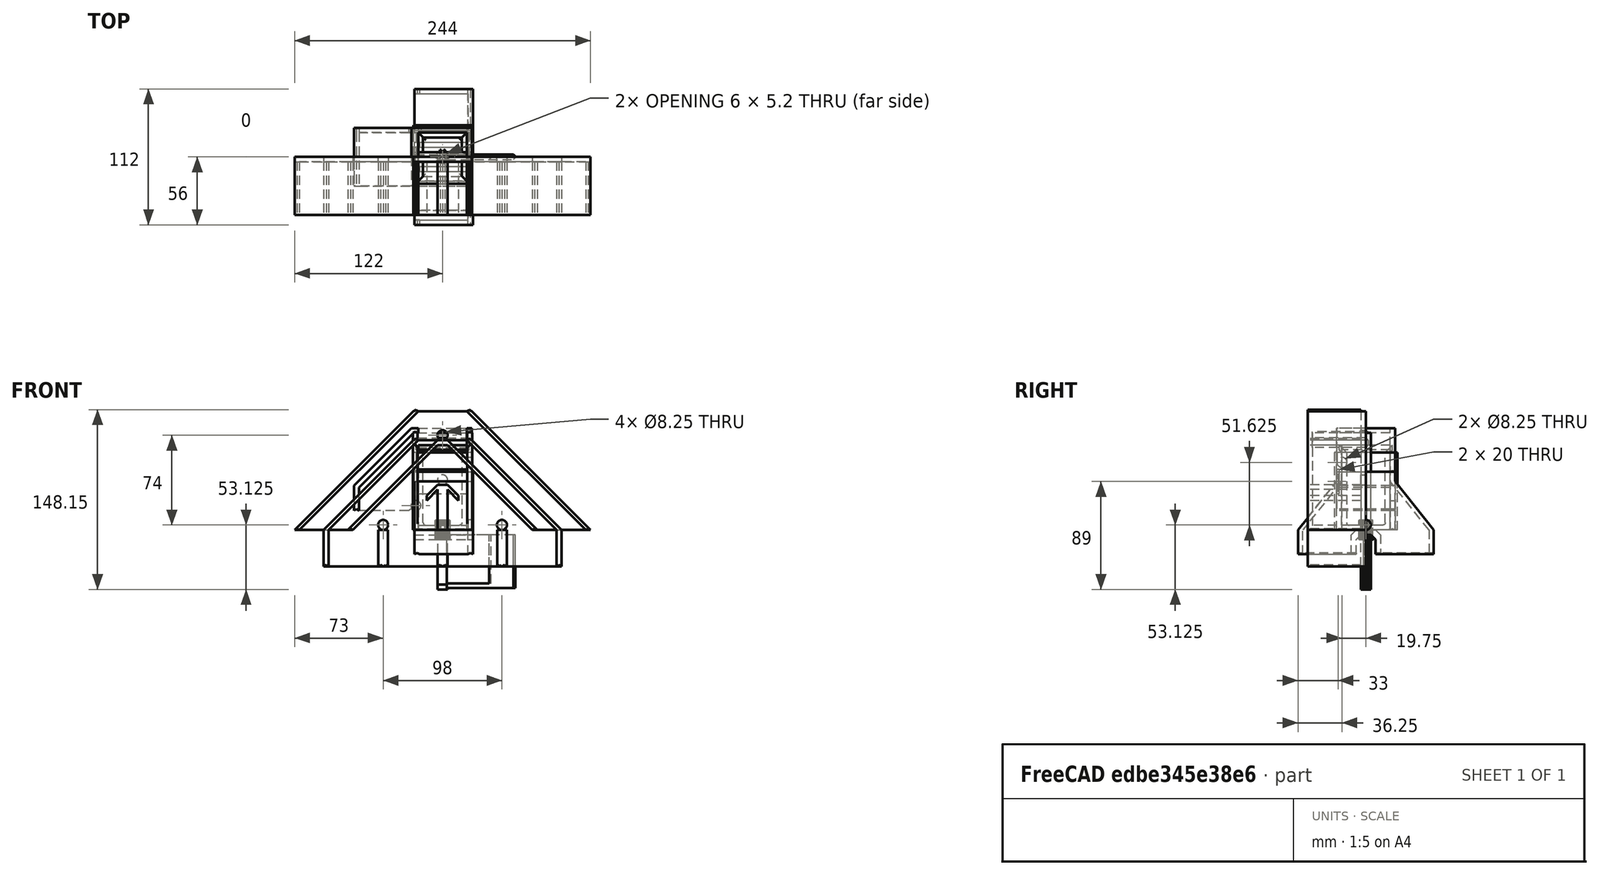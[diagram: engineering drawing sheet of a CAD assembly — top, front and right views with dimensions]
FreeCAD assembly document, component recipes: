
FREECAD ASSEMBLY — COMPONENT RECIPES ("Sorter")

This assembly document has 58 components, labeled P0..P57 below (a component is one placed body or linked part). 0 of them carry a construction recipe — the FreeCAD feature program that regenerates the part from scratch, quoted from this document or its linked companion documents; the rest are supplied as boundary geometry only. No exploded tour is included for this assembly.
COMPONENT P0 — geometry summary ("Bin001"; no construction recipe available for this part):
  bounding box: 70.0 x 44.0 x 44.0 mm
  tessellated surface: 356 triangles
  volume: 43396 mm^3 (32% of its bounding box)
  symmetry: 2-fold rotationally symmetric about the z axis; mirror-symmetric across its y mid-plane
COMPONENT P1 — geometry summary ("Bin002"; no construction recipe available for this part):
  bounding box: 70.0 x 44.0 x 44.0 mm
  tessellated surface: 356 triangles
  volume: 43396 mm^3 (32% of its bounding box)
  symmetry: 2-fold rotationally symmetric about the z axis; mirror-symmetric across its y mid-plane
COMPONENT P2 — geometry summary ("Bin003"; no construction recipe available for this part):
  bounding box: 70.0 x 44.0 x 44.0 mm
  tessellated surface: 356 triangles
  volume: 43396 mm^3 (32% of its bounding box)
  symmetry: 2-fold rotationally symmetric about the z axis; mirror-symmetric across its y mid-plane
COMPONENT P3 — geometry summary ("Bin004"; no construction recipe available for this part):
  bounding box: 70.0 x 44.0 x 44.0 mm
  tessellated surface: 356 triangles
  volume: 43396 mm^3 (32% of its bounding box)
  symmetry: 2-fold rotationally symmetric about the z axis; mirror-symmetric across its y mid-plane
COMPONENT P4 — geometry summary ("Bin005"; no construction recipe available for this part):
  bounding box: 70.0 x 44.0 x 44.0 mm
  tessellated surface: 356 triangles
  volume: 43396 mm^3 (32% of its bounding box)
  symmetry: 2-fold rotationally symmetric about the z axis; mirror-symmetric across its y mid-plane
COMPONENT P5 — geometry summary ("Bin006"; no construction recipe available for this part):
  bounding box: 70.0 x 44.0 x 44.0 mm
  tessellated surface: 356 triangles
  volume: 43396 mm^3 (32% of its bounding box)
  symmetry: 2-fold rotationally symmetric about the z axis; mirror-symmetric across its y mid-plane
COMPONENT P6 — geometry summary ("Bin007"; no construction recipe available for this part):
  bounding box: 70.0 x 44.0 x 44.0 mm
  tessellated surface: 356 triangles
  volume: 43396 mm^3 (32% of its bounding box)
  symmetry: 2-fold rotationally symmetric about the z axis; mirror-symmetric across its y mid-plane
COMPONENT P7 — geometry summary ("Bin008"; no construction recipe available for this part):
  bounding box: 70.0 x 44.0 x 44.0 mm
  tessellated surface: 356 triangles
  volume: 43396 mm^3 (32% of its bounding box)
  symmetry: 2-fold rotationally symmetric about the z axis; mirror-symmetric across its y mid-plane
COMPONENT P8 — geometry summary ("Bin009"; no construction recipe available for this part):
  bounding box: 70.0 x 44.0 x 44.0 mm
  tessellated surface: 356 triangles
  volume: 43396 mm^3 (32% of its bounding box)
  symmetry: 2-fold rotationally symmetric about the z axis; mirror-symmetric across its y mid-plane
COMPONENT P9 — geometry summary ("Bin010"; no construction recipe available for this part):
  bounding box: 70.0 x 44.0 x 44.0 mm
  tessellated surface: 356 triangles
  volume: 43396 mm^3 (32% of its bounding box)
  symmetry: 2-fold rotationally symmetric about the z axis; mirror-symmetric across its y mid-plane
COMPONENT P10 — geometry summary ("Bin011"; no construction recipe available for this part):
  bounding box: 70.0 x 44.0 x 44.0 mm
  tessellated surface: 356 triangles
  volume: 43396 mm^3 (32% of its bounding box)
  symmetry: 2-fold rotationally symmetric about the z axis; mirror-symmetric across its y mid-plane
COMPONENT P11 — geometry summary ("Bin012"; no construction recipe available for this part):
  bounding box: 70.0 x 44.0 x 44.0 mm
  tessellated surface: 356 triangles
  volume: 43396 mm^3 (32% of its bounding box)
  symmetry: 2-fold rotationally symmetric about the z axis; mirror-symmetric across its y mid-plane
COMPONENT P12 — geometry summary ("Bin013"; no construction recipe available for this part):
  bounding box: 70.0 x 44.0 x 44.0 mm
  tessellated surface: 356 triangles
  volume: 43396 mm^3 (32% of its bounding box)
  symmetry: 2-fold rotationally symmetric about the z axis; mirror-symmetric across its y mid-plane
COMPONENT P13 — geometry summary ("Bin014"; no construction recipe available for this part):
  bounding box: 70.0 x 44.0 x 44.0 mm
  tessellated surface: 356 triangles
  volume: 43396 mm^3 (32% of its bounding box)
  symmetry: 2-fold rotationally symmetric about the z axis; mirror-symmetric across its y mid-plane
COMPONENT P14 — geometry summary ("Bin015"; no construction recipe available for this part):
  bounding box: 70.0 x 44.0 x 44.0 mm
  tessellated surface: 356 triangles
  volume: 43396 mm^3 (32% of its bounding box)
  symmetry: 2-fold rotationally symmetric about the z axis; mirror-symmetric across its y mid-plane
COMPONENT P15 — geometry summary ("Bin016"; no construction recipe available for this part):
  bounding box: 70.0 x 44.0 x 44.0 mm
  tessellated surface: 356 triangles
  volume: 43396 mm^3 (32% of its bounding box)
  symmetry: 2-fold rotationally symmetric about the z axis; mirror-symmetric across its y mid-plane
COMPONENT P16 — geometry summary ("Bin017"; no construction recipe available for this part):
  bounding box: 70.0 x 44.0 x 44.0 mm
  tessellated surface: 356 triangles
  volume: 43396 mm^3 (32% of its bounding box)
  symmetry: 2-fold rotationally symmetric about the z axis; mirror-symmetric across its y mid-plane
COMPONENT P17 — geometry summary ("Bin Holder001"; no construction recipe available for this part):
  bounding box: 81.2 x 49.0 x 48.0 mm
  tessellated surface: 164 triangles
  volume: 49705 mm^3 (26% of its bounding box)
  symmetry: mirror-symmetric across its x mid-plane
COMPONENT P18 — geometry summary ("Bin Holder002"; no construction recipe available for this part):
  bounding box: 81.2 x 49.0 x 48.0 mm
  tessellated surface: 164 triangles
  volume: 49705 mm^3 (26% of its bounding box)
  symmetry: mirror-symmetric across its x mid-plane
COMPONENT P19 — geometry summary ("Bin Holder003"; no construction recipe available for this part):
  bounding box: 81.2 x 49.0 x 48.0 mm
  tessellated surface: 164 triangles
  volume: 49705 mm^3 (26% of its bounding box)
  symmetry: mirror-symmetric across its x mid-plane
COMPONENT P20 — geometry summary ("Bin Holder004"; no construction recipe available for this part):
  bounding box: 81.2 x 49.0 x 48.0 mm
  tessellated surface: 164 triangles
  volume: 49705 mm^3 (26% of its bounding box)
  symmetry: mirror-symmetric across its x mid-plane
COMPONENT P21 — geometry summary ("Bin Holder005"; no construction recipe available for this part):
  bounding box: 81.2 x 49.0 x 48.0 mm
  tessellated surface: 164 triangles
  volume: 49705 mm^3 (26% of its bounding box)
  symmetry: mirror-symmetric across its x mid-plane
COMPONENT P22 — geometry summary ("Bin Holder006"; no construction recipe available for this part):
  bounding box: 81.2 x 49.0 x 48.0 mm
  tessellated surface: 164 triangles
  volume: 49705 mm^3 (26% of its bounding box)
  symmetry: mirror-symmetric across its x mid-plane
COMPONENT P23 — geometry summary ("Bin Holder007"; no construction recipe available for this part):
  bounding box: 81.2 x 49.0 x 48.0 mm
  tessellated surface: 164 triangles
  volume: 49705 mm^3 (26% of its bounding box)
  symmetry: mirror-symmetric across its x mid-plane
COMPONENT P24 — geometry summary ("Bin Holder008"; no construction recipe available for this part):
  bounding box: 81.2 x 49.0 x 48.0 mm
  tessellated surface: 164 triangles
  volume: 49705 mm^3 (26% of its bounding box)
  symmetry: mirror-symmetric across its x mid-plane
COMPONENT P25 — geometry summary ("Bin Holder009"; no construction recipe available for this part):
  bounding box: 81.2 x 49.0 x 48.0 mm
  tessellated surface: 164 triangles
  volume: 49705 mm^3 (26% of its bounding box)
  symmetry: mirror-symmetric across its x mid-plane
COMPONENT P26 — geometry summary ("Bin Holder010"; no construction recipe available for this part):
  bounding box: 81.2 x 49.0 x 48.0 mm
  tessellated surface: 164 triangles
  volume: 49705 mm^3 (26% of its bounding box)
  symmetry: mirror-symmetric across its x mid-plane
COMPONENT P27 — geometry summary ("Bin Holder011"; no construction recipe available for this part):
  bounding box: 81.2 x 49.0 x 48.0 mm
  tessellated surface: 164 triangles
  volume: 49705 mm^3 (26% of its bounding box)
  symmetry: mirror-symmetric across its x mid-plane
COMPONENT P28 — geometry summary ("Bin Holder012"; no construction recipe available for this part):
  bounding box: 81.2 x 49.0 x 48.0 mm
  tessellated surface: 164 triangles
  volume: 49705 mm^3 (26% of its bounding box)
  symmetry: mirror-symmetric across its x mid-plane
COMPONENT P29 — geometry summary ("Bin Holder013"; no construction recipe available for this part):
  bounding box: 81.2 x 49.0 x 48.0 mm
  tessellated surface: 164 triangles
  volume: 49705 mm^3 (26% of its bounding box)
  symmetry: mirror-symmetric across its x mid-plane
COMPONENT P30 — geometry summary ("Bin Holder014"; no construction recipe available for this part):
  bounding box: 81.2 x 49.0 x 48.0 mm
  tessellated surface: 164 triangles
  volume: 49705 mm^3 (26% of its bounding box)
  symmetry: mirror-symmetric across its x mid-plane
COMPONENT P31 — geometry summary ("Bin Holder015"; no construction recipe available for this part):
  bounding box: 81.2 x 49.0 x 48.0 mm
  tessellated surface: 164 triangles
  volume: 49705 mm^3 (26% of its bounding box)
  symmetry: mirror-symmetric across its x mid-plane
COMPONENT P32 — geometry summary ("Bin Holder016"; no construction recipe available for this part):
  bounding box: 81.2 x 49.0 x 48.0 mm
  tessellated surface: 164 triangles
  volume: 49705 mm^3 (26% of its bounding box)
  symmetry: mirror-symmetric across its x mid-plane
COMPONENT P33 — geometry summary ("Bin Holder017"; no construction recipe available for this part):
  bounding box: 81.2 x 49.0 x 48.0 mm
  tessellated surface: 164 triangles
  volume: 49705 mm^3 (26% of its bounding box)
  symmetry: mirror-symmetric across its x mid-plane
COMPONENT P34 — geometry summary ("Flap001"; no construction recipe available for this part):
  bounding box: 52.0 x 44.0 x 8.0 mm
  tessellated surface: 628 triangles
  volume: 8118 mm^3 (44% of its bounding box)
  symmetry: mirror-symmetric across its x mid-plane
COMPONENT P35 — geometry summary ("Flap002"; no construction recipe available for this part):
  bounding box: 52.0 x 44.0 x 8.0 mm
  tessellated surface: 628 triangles
  volume: 8118 mm^3 (44% of its bounding box)
  symmetry: mirror-symmetric across its x mid-plane
COMPONENT P36 — geometry summary ("Flap003"; no construction recipe available for this part):
  bounding box: 52.0 x 44.0 x 8.0 mm
  tessellated surface: 628 triangles
  volume: 8118 mm^3 (44% of its bounding box)
  symmetry: mirror-symmetric across its x mid-plane
COMPONENT P37 — geometry summary ("Flap004"; no construction recipe available for this part):
  bounding box: 52.0 x 44.0 x 8.0 mm
  tessellated surface: 628 triangles
  volume: 8118 mm^3 (44% of its bounding box)
  symmetry: mirror-symmetric across its x mid-plane
COMPONENT P38 — geometry summary ("Flap005"; no construction recipe available for this part):
  bounding box: 52.0 x 44.0 x 8.0 mm
  tessellated surface: 628 triangles
  volume: 8118 mm^3 (44% of its bounding box)
  symmetry: mirror-symmetric across its x mid-plane
COMPONENT P39 — geometry summary ("Flap006"; no construction recipe available for this part):
  bounding box: 52.0 x 44.0 x 8.0 mm
  tessellated surface: 628 triangles
  volume: 8118 mm^3 (44% of its bounding box)
  symmetry: mirror-symmetric across its x mid-plane
COMPONENT P40 — geometry summary ("Flap007"; no construction recipe available for this part):
  bounding box: 52.0 x 44.0 x 8.0 mm
  tessellated surface: 628 triangles
  volume: 8118 mm^3 (44% of its bounding box)
  symmetry: mirror-symmetric across its x mid-plane
COMPONENT P41 — geometry summary ("Flap008"; no construction recipe available for this part):
  bounding box: 52.0 x 44.0 x 8.0 mm
  tessellated surface: 628 triangles
  volume: 8118 mm^3 (44% of its bounding box)
  symmetry: mirror-symmetric across its x mid-plane
COMPONENT P42 — geometry summary ("Flap009"; no construction recipe available for this part):
  bounding box: 52.0 x 44.0 x 8.0 mm
  tessellated surface: 628 triangles
  volume: 8118 mm^3 (44% of its bounding box)
  symmetry: mirror-symmetric across its x mid-plane
COMPONENT P43 — geometry summary ("Flap010"; no construction recipe available for this part):
  bounding box: 52.0 x 44.0 x 8.0 mm
  tessellated surface: 628 triangles
  volume: 8118 mm^3 (44% of its bounding box)
  symmetry: mirror-symmetric across its x mid-plane
COMPONENT P44 — geometry summary ("Flap011"; no construction recipe available for this part):
  bounding box: 52.0 x 44.0 x 8.0 mm
  tessellated surface: 628 triangles
  volume: 8118 mm^3 (44% of its bounding box)
  symmetry: mirror-symmetric across its x mid-plane
COMPONENT P45 — geometry summary ("Flap012"; no construction recipe available for this part):
  bounding box: 52.0 x 44.0 x 8.0 mm
  tessellated surface: 628 triangles
  volume: 8118 mm^3 (44% of its bounding box)
  symmetry: mirror-symmetric across its x mid-plane
COMPONENT P46 — geometry summary ("Flap013"; no construction recipe available for this part):
  bounding box: 52.0 x 44.0 x 8.0 mm
  tessellated surface: 628 triangles
  volume: 8118 mm^3 (44% of its bounding box)
  symmetry: mirror-symmetric across its x mid-plane
COMPONENT P47 — geometry summary ("Flap014"; no construction recipe available for this part):
  bounding box: 52.0 x 44.0 x 8.0 mm
  tessellated surface: 628 triangles
  volume: 8118 mm^3 (44% of its bounding box)
  symmetry: mirror-symmetric across its x mid-plane
COMPONENT P48 — geometry summary ("Flap015"; no construction recipe available for this part):
  bounding box: 52.0 x 44.0 x 8.0 mm
  tessellated surface: 628 triangles
  volume: 8118 mm^3 (44% of its bounding box)
  symmetry: mirror-symmetric across its x mid-plane
COMPONENT P49 — geometry summary ("Reject Flap001"; no construction recipe available for this part):
  bounding box: 64.0 x 57.0 x 8.0 mm
  tessellated surface: 628 triangles
  volume: 12438 mm^3 (43% of its bounding box)
COMPONENT P50 — geometry summary ("Reject Path001"; no construction recipe available for this part):
  bounding box: 97.0 x 84.0 x 48.0 mm
  tessellated surface: 612 triangles
  volume: 57960 mm^3 (15% of its bounding box)
COMPONENT P51 — geometry summary ("Stage 1 Paths001"; no construction recipe available for this part):
  bounding box: 112.0 x 69.2 x 48.0 mm
  tessellated surface: 698 triangles
  volume: 55757 mm^3 (15% of its bounding box)
  symmetry: mirror-symmetric across its y mid-plane
COMPONENT P52 — geometry summary ("Stage 2 Paths001"; no construction recipe available for this part):
  bounding box: 244.0 x 99.2 x 48.0 mm
  tessellated surface: 622 triangles
  volume: 96223 mm^3 (8% of its bounding box)
  symmetry: mirror-symmetric across its x mid-plane
COMPONENT P53 — geometry summary ("Stage 2 Paths002"; no construction recipe available for this part):
  bounding box: 244.0 x 99.2 x 48.0 mm
  tessellated surface: 622 triangles
  volume: 96223 mm^3 (8% of its bounding box)
  symmetry: mirror-symmetric across its x mid-plane
COMPONENT P54 — geometry summary ("Stage 3 Paths001"; no construction recipe available for this part):
  bounding box: 196.0 x 105.2 x 48.0 mm
  tessellated surface: 1,744 triangles
  volume: 143032 mm^3 (14% of its bounding box)
COMPONENT P55 — geometry summary ("Stage 3 Paths002"; no construction recipe available for this part):
  bounding box: 196.0 x 105.2 x 48.0 mm
  tessellated surface: 1,744 triangles
  volume: 143032 mm^3 (14% of its bounding box)
COMPONENT P56 — geometry summary ("Stage 3 Paths003"; no construction recipe available for this part):
  bounding box: 196.0 x 105.2 x 48.0 mm
  tessellated surface: 1,744 triangles
  volume: 143032 mm^3 (14% of its bounding box)
COMPONENT P57 — geometry summary ("Stage 3 Paths004"; no construction recipe available for this part):
  bounding box: 196.0 x 105.2 x 48.0 mm
  tessellated surface: 1,744 triangles
  volume: 143032 mm^3 (14% of its bounding box)
PROVENANCE & LICENSES
A FreeCAD (.FCStd) document from a public repository crawl; recipes are the document's own serialized feature recipes (and, for linked parts, companion documents' recipes).
License: gpl-3.0.
